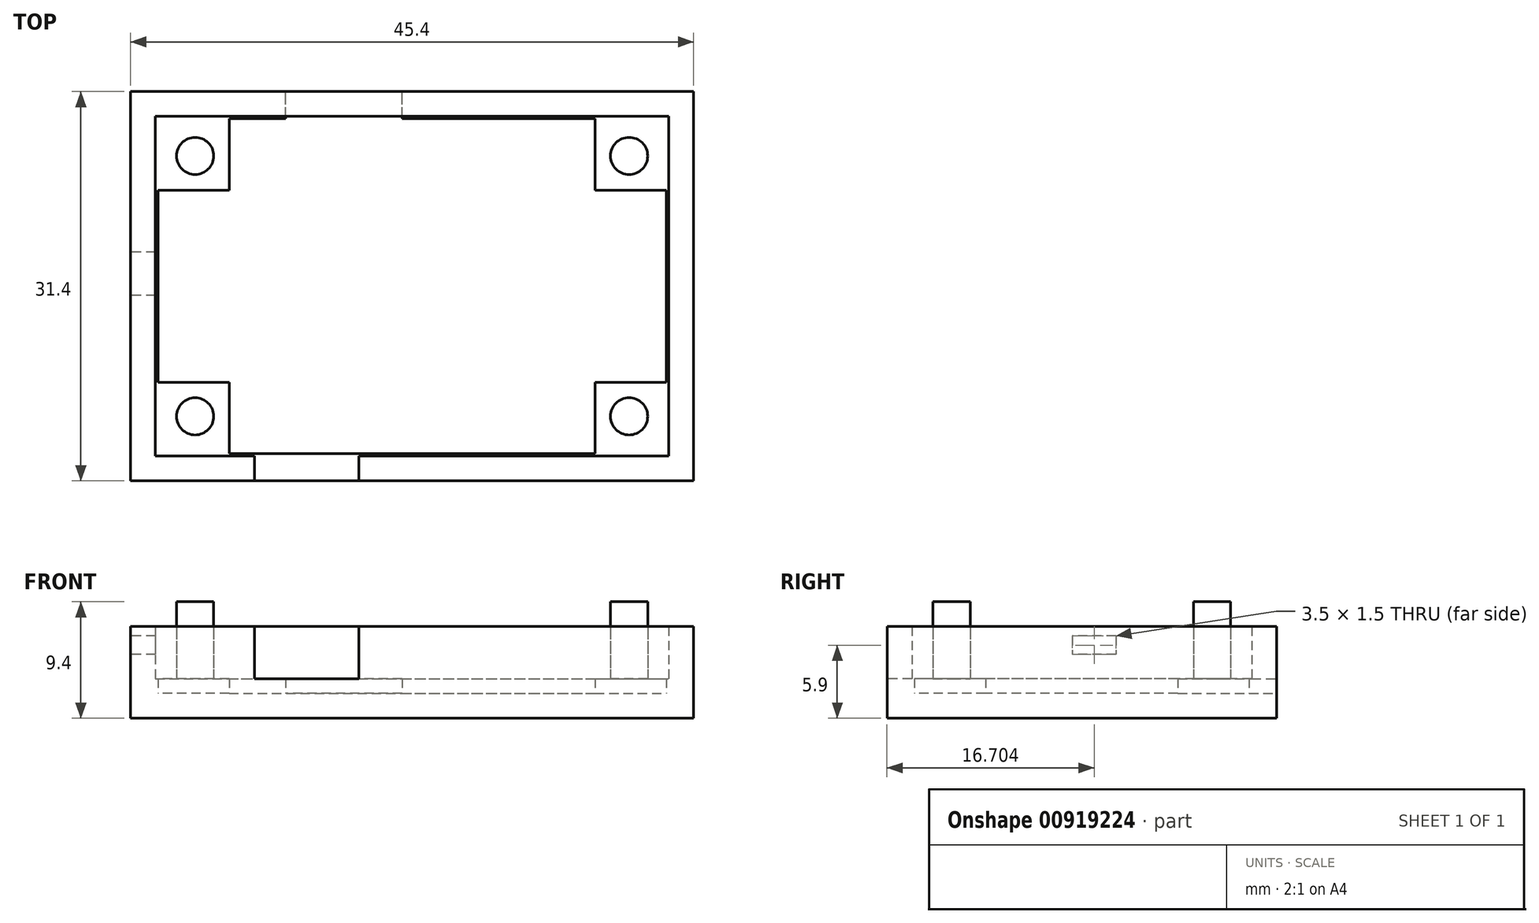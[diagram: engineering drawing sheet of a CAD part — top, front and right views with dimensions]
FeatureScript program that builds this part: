
annotation { "Feature Type Name" : "Feature", "Feature Type Description" : "" }
export const myFeature = defineFeature(function(context is Context, id is Id, definition is map)
    precondition{}
    {
        {
            assignVariable(context, id + "F0", {"name" : "thickness", "anyValue" : 2});
        }
        {
            assignVariable(context, id + "F1", {"name" : "padding", "anyValue" : 0.2});
        }
        {
            var Q0;
            Q0=qCreatedBy(makeId("Top.planeOp"),FACE);
            var sketch = newSketch(context, id + "F2", { "sketchPlane" : qUnion([Q0])});
            skLineSegment(sketch, "E0.bottom", {"start": v(-15.97, 10.74) * mm, "end": v(25.03, 10.74) * mm});
            skLineSegment(sketch, "E0.top", {"start": v(-15.97, -16.26) * mm, "end": v(25.03, -16.26) * mm});
            skLineSegment(sketch, "E0.left", {"start": v(-15.97, 10.74) * mm, "end": v(-15.97, -16.26) * mm});
            skLineSegment(sketch, "E0.right", {"start": v(25.03, 10.74) * mm, "end": v(25.03, -16.26) * mm});
            skCircle(sketch, "E1", {"center": v(-12.97, 7.74) * mm, "radius": 1.75 * mm});
            skPoint(sketch, "E2", {"position": v(25.03, -2.76) * mm});
            skCircle(sketch, "E3", {"center": v(22.03, 7.74) * mm, "radius": 1.75 * mm});
            skCircle(sketch, "E4", {"center": v(22.03, -13.26) * mm, "radius": 1.75 * mm});
            skCircle(sketch, "E5", {"center": v(-12.97, -13.26) * mm, "radius": 1.75 * mm});
            skLineSegment(sketch, "E6.bottom", {"start": v(-15.97, 10.74) * mm, "end": v(-10.22, 10.74) * mm});
            skLineSegment(sketch, "E6.top", {"start": v(-15.97, 5) * mm, "end": v(-10.22, 5) * mm});
            skLineSegment(sketch, "E6.left", {"start": v(-15.97, 10.74) * mm, "end": v(-15.97, 5) * mm});
            skLineSegment(sketch, "E6.right", {"start": v(-10.22, 10.74) * mm, "end": v(-10.22, 5) * mm});
            skLineSegment(sketch, "E7.bottom", {"start": v(19.28, 5) * mm, "end": v(25.03, 5) * mm});
            skLineSegment(sketch, "E7.top", {"start": v(19.28, 10.74) * mm, "end": v(25.03, 10.74) * mm});
            skLineSegment(sketch, "E7.left", {"start": v(19.28, 5) * mm, "end": v(19.28, 10.74) * mm});
            skLineSegment(sketch, "E7.right", {"start": v(25.03, 5) * mm, "end": v(25.03, 10.74) * mm});
            skLineSegment(sketch, "E8.bottom", {"start": v(19.28, -10.5) * mm, "end": v(25.03, -10.5) * mm});
            skLineSegment(sketch, "E8.top", {"start": v(19.28, -16.26) * mm, "end": v(25.03, -16.26) * mm});
            skLineSegment(sketch, "E8.left", {"start": v(19.28, -10.5) * mm, "end": v(19.28, -16.26) * mm});
            skLineSegment(sketch, "E8.right", {"start": v(25.03, -10.5) * mm, "end": v(25.03, -16.26) * mm});
            skLineSegment(sketch, "E9.bottom", {"start": v(-10.22, -10.5) * mm, "end": v(-15.97, -10.5) * mm});
            skLineSegment(sketch, "E9.top", {"start": v(-10.22, -16.26) * mm, "end": v(-15.97, -16.26) * mm});
            skLineSegment(sketch, "E9.left", {"start": v(-10.22, -10.5) * mm, "end": v(-10.22, -16.26) * mm});
            skLineSegment(sketch, "E9.right", {"start": v(-15.97, -10.5) * mm, "end": v(-15.97, -16.26) * mm});
            skLineSegment(sketch, "E10.bottom", {"start": v(-16.17, 10.94) * mm, "end": v(25.23, 10.94) * mm});
            skLineSegment(sketch, "E10.top", {"start": v(-16.17, -16.46) * mm, "end": v(25.23, -16.46) * mm});
            skLineSegment(sketch, "E10.left", {"start": v(-16.17, 10.94) * mm, "end": v(-16.17, -16.46) * mm});
            skLineSegment(sketch, "E10.right", {"start": v(25.23, 10.94) * mm, "end": v(25.23, -16.46) * mm});
            skLineSegment(sketch, "E11", {"start": v(19.28, 10.74) * mm, "end": v(19.28, 10.94) * mm});
            skLineSegment(sketch, "E12", {"start": v(25.03, 5) * mm, "end": v(25.23, 5) * mm});
            skLineSegment(sketch, "E13", {"start": v(-10.22, 10.74) * mm, "end": v(-10.22, 10.94) * mm});
            skLineSegment(sketch, "E14", {"start": v(-15.97, 5) * mm, "end": v(-16.17, 5) * mm});
            skLineSegment(sketch, "E15", {"start": v(-10.22, -16.26) * mm, "end": v(-10.22, -16.46) * mm});
            skLineSegment(sketch, "E16", {"start": v(-15.97, -10.5) * mm, "end": v(-16.17, -10.5) * mm});
            skLineSegment(sketch, "E17", {"start": v(19.28, -16.26) * mm, "end": v(19.28, -16.46) * mm});
            skLineSegment(sketch, "E18", {"start": v(25.03, -10.5) * mm, "end": v(25.23, -10.5) * mm});
            skLineSegment(sketch, "E19.bottom", {"start": v(-18.17, 12.94) * mm, "end": v(27.23, 12.94) * mm});
            skLineSegment(sketch, "E19.top", {"start": v(-18.17, -18.46) * mm, "end": v(27.23, -18.46) * mm});
            skLineSegment(sketch, "E19.left", {"start": v(-18.17, 12.94) * mm, "end": v(-18.17, -18.46) * mm});
            skLineSegment(sketch, "E19.right", {"start": v(27.23, 12.94) * mm, "end": v(27.23, -18.46) * mm});
            skSolve(sketch);
        }
        {
            var Q0;
            Q0=makeQuery(id+"F2.imprint","IMPRINT",FACE,{"disambiguationData":[TD([[makeQuery(id+"F2.imprint","IMPRINT",EDGE,{"derivedFrom":sQuery(id+"F2.wireOp",EDGE,"E3")}),-1.0]])]});
            var Q1;
            Q1=makeQuery(id+"F2.imprint","IMPRINT",FACE,{"disambiguationData":[TD([[makeQuery(id+"F2.imprint","IMPRINT",EDGE,{"derivedFrom":sQuery(id+"F2.wireOp",EDGE,"E1")}),-1.0]])]});
            var Q2;
            Q2=makeQuery(id+"F2.imprint","IMPRINT",FACE,{"disambiguationData":[TD([[makeQuery(id+"F2.imprint","IMPRINT",EDGE,{"derivedFrom":sQuery(id+"F2.wireOp",EDGE,"E1")}),1.0]])]});
            var Q3;
            Q3=makeQuery(id+"F2.imprint","IMPRINT",FACE,{"disambiguationData":[TD([[makeQuery(id+"F2.imprint","IMPRINT",EDGE,{"derivedFrom":sQuery(id+"F2.wireOp",EDGE,"E3")}),1.0]])]});
            var Q4;
            Q4=makeQuery(id+"F2.imprint","IMPRINT",FACE,{"disambiguationData":[TD([[makeQuery(id+"F2.imprint","IMPRINT",EDGE,{"derivedFrom":sQuery(id+"F2.wireOp",EDGE,"E4")}),1.0]])]});
            var Q5;
            Q5=makeQuery(id+"F2.imprint","IMPRINT",FACE,{"disambiguationData":[TD([[makeQuery(id+"F2.imprint","IMPRINT",EDGE,{"derivedFrom":sQuery(id+"F2.wireOp",EDGE,"E4")}),-1.0]])]});
            var Q6;
            Q6=makeQuery(id+"F2.imprint","IMPRINT",FACE,{"disambiguationData":[TD([[makeQuery(id+"F2.imprint","IMPRINT",EDGE,{"derivedFrom":sQuery(id+"F2.wireOp",EDGE,"E5")}),1.0]])]});
            var Q7;
            Q7=makeQuery(id+"F2.imprint","IMPRINT",FACE,{"disambiguationData":[TD([[makeQuery(id+"F2.imprint","IMPRINT",EDGE,{"derivedFrom":sQuery(id+"F2.wireOp",EDGE,"E5")}),-1.0]])]});
            var Q8;
            {var subQ0=sQuery(id+"F2.wireOp",EDGE,"E15");Q8=makeQuery(id+"F2.imprint","IMPRINT",FACE,{"disambiguationData":[TD([[makeQuery(id+"F2.imprint","IMPRINT",EDGE,{"derivedFrom":subQ0}),1.0]])]});}
            var Q9;
            {var subQ4=sQuery(id+"F2.wireOp",EDGE,"E15");Q9=makeQuery(id+"F2.imprint","IMPRINT",FACE,{"disambiguationData":[TD([[makeQuery(id+"F2.imprint","IMPRINT",EDGE,{"derivedFrom":subQ4}),-1.0]])]});}
            var Q10;
            {var subQ0=sQuery(id+"F2.wireOp",EDGE,"E14");Q10=makeQuery(id+"F2.imprint","IMPRINT",FACE,{"disambiguationData":[TD([[makeQuery(id+"F2.imprint","IMPRINT",EDGE,{"derivedFrom":subQ0}),1.0]])]});}
            var Q11;
            {var subQ0=sQuery(id+"F2.wireOp",EDGE,"E13");Q11=makeQuery(id+"F2.imprint","IMPRINT",FACE,{"disambiguationData":[TD([[makeQuery(id+"F2.imprint","IMPRINT",EDGE,{"derivedFrom":subQ0}),1.0]])]});}
            var Q12;
            {var subQ2=sQuery(id+"F2.wireOp",EDGE,"E11");Q12=makeQuery(id+"F2.imprint","IMPRINT",FACE,{"disambiguationData":[TD([[makeQuery(id+"F2.imprint","IMPRINT",EDGE,{"derivedFrom":subQ2}),1.0]])]});}
            var Q13;
            {var subQ0=sQuery(id+"F2.wireOp",EDGE,"E12");Q13=makeQuery(id+"F2.imprint","IMPRINT",FACE,{"disambiguationData":[TD([[makeQuery(id+"F2.imprint","IMPRINT",EDGE,{"derivedFrom":subQ0}),-1.0]])]});}
            var Q14;
            {var subQ3=sQuery(id+"F2.wireOp",EDGE,"E17");Q14=makeQuery(id+"F2.imprint","IMPRINT",FACE,{"disambiguationData":[TD([[makeQuery(id+"F2.imprint","IMPRINT",EDGE,{"derivedFrom":subQ3}),1.0]])]});}
            var Q15;
            Q15=makeQuery(id+"F2.imprint","IMPRINT",FACE,{"disambiguationData":[TD([[makeQuery(id+"F2.imprint","IMPRINT",EDGE,{"derivedFrom":sQuery(id+"F2.wireOp",EDGE,"E19.bottom")}),-1.0]])]});
            var Q16;
            {var subQ4=sQuery(id+"F2.wireOp",EDGE,"E11");Q16=makeQuery(id+"F2.imprint","IMPRINT",FACE,{"disambiguationData":[TD([[makeQuery(id+"F2.imprint","IMPRINT",EDGE,{"derivedFrom":subQ4}),-1.0]])]});}
            extrude(context, id + "F3", {"entities" : qUnion([Q0, Q1, Q2, Q3, Q4, Q5, Q6, Q7, Q8, Q9, Q10, Q11, Q12, Q13, Q14, Q15, Q16]), "depth" : (1 + getVariable(context, 'padding')) * mm, "offsetDistance" : 25 * mm});
        }
        {
            var Q0;
            Q0=makeQuery(id+"F2.imprint","IMPRINT",FACE,{"disambiguationData":[TD([[makeQuery(id+"F2.imprint","IMPRINT",EDGE,{"derivedFrom":sQuery(id+"F2.wireOp",EDGE,"E1")}),1.0]])]});
            var Q1;
            Q1=makeQuery(id+"F2.imprint","IMPRINT",FACE,{"disambiguationData":[TD([[makeQuery(id+"F2.imprint","IMPRINT",EDGE,{"derivedFrom":sQuery(id+"F2.wireOp",EDGE,"E1")}),-1.0]])]});
            var Q2;
            {var subQ0=sQuery(id+"F2.wireOp",EDGE,"E13");Q2=makeQuery(id+"F2.imprint","IMPRINT",FACE,{"disambiguationData":[TD([[makeQuery(id+"F2.imprint","IMPRINT",EDGE,{"derivedFrom":subQ0}),1.0]])]});}
            var Q3;
            {var subQ2=sQuery(id+"F2.wireOp",EDGE,"E11");Q3=makeQuery(id+"F2.imprint","IMPRINT",FACE,{"disambiguationData":[TD([[makeQuery(id+"F2.imprint","IMPRINT",EDGE,{"derivedFrom":subQ2}),1.0]])]});}
            var Q4;
            {var subQ0=sQuery(id+"F2.wireOp",EDGE,"E14");Q4=makeQuery(id+"F2.imprint","IMPRINT",FACE,{"disambiguationData":[TD([[makeQuery(id+"F2.imprint","IMPRINT",EDGE,{"derivedFrom":subQ0}),1.0]])]});}
            var Q5;
            {var subQ4=sQuery(id+"F2.wireOp",EDGE,"E15");Q5=makeQuery(id+"F2.imprint","IMPRINT",FACE,{"disambiguationData":[TD([[makeQuery(id+"F2.imprint","IMPRINT",EDGE,{"derivedFrom":subQ4}),-1.0]])]});}
            var Q6;
            {var subQ0=sQuery(id+"F2.wireOp",EDGE,"E15");Q6=makeQuery(id+"F2.imprint","IMPRINT",FACE,{"disambiguationData":[TD([[makeQuery(id+"F2.imprint","IMPRINT",EDGE,{"derivedFrom":subQ0}),1.0]])]});}
            var Q7;
            Q7=makeQuery(id+"F2.imprint","IMPRINT",FACE,{"disambiguationData":[TD([[makeQuery(id+"F2.imprint","IMPRINT",EDGE,{"derivedFrom":sQuery(id+"F2.wireOp",EDGE,"E5")}),1.0]])]});
            var Q8;
            Q8=makeQuery(id+"F2.imprint","IMPRINT",FACE,{"disambiguationData":[TD([[makeQuery(id+"F2.imprint","IMPRINT",EDGE,{"derivedFrom":sQuery(id+"F2.wireOp",EDGE,"E5")}),-1.0]])]});
            var Q9;
            Q9=makeQuery(id+"F2.imprint","IMPRINT",FACE,{"disambiguationData":[TD([[makeQuery(id+"F2.imprint","IMPRINT",EDGE,{"derivedFrom":sQuery(id+"F2.wireOp",EDGE,"E4")}),-1.0]])]});
            var Q10;
            Q10=makeQuery(id+"F2.imprint","IMPRINT",FACE,{"disambiguationData":[TD([[makeQuery(id+"F2.imprint","IMPRINT",EDGE,{"derivedFrom":sQuery(id+"F2.wireOp",EDGE,"E4")}),1.0]])]});
            var Q11;
            {var subQ3=sQuery(id+"F2.wireOp",EDGE,"E17");Q11=makeQuery(id+"F2.imprint","IMPRINT",FACE,{"disambiguationData":[TD([[makeQuery(id+"F2.imprint","IMPRINT",EDGE,{"derivedFrom":subQ3}),1.0]])]});}
            var Q12;
            Q12=makeQuery(id+"F2.imprint","IMPRINT",FACE,{"disambiguationData":[TD([[makeQuery(id+"F2.imprint","IMPRINT",EDGE,{"derivedFrom":sQuery(id+"F2.wireOp",EDGE,"E19.bottom")}),-1.0]])]});
            var Q13;
            {var subQ0=sQuery(id+"F2.wireOp",EDGE,"E12");Q13=makeQuery(id+"F2.imprint","IMPRINT",FACE,{"disambiguationData":[TD([[makeQuery(id+"F2.imprint","IMPRINT",EDGE,{"derivedFrom":subQ0}),-1.0]])]});}
            var Q14;
            {var subQ4=sQuery(id+"F2.wireOp",EDGE,"E11");Q14=makeQuery(id+"F2.imprint","IMPRINT",FACE,{"disambiguationData":[TD([[makeQuery(id+"F2.imprint","IMPRINT",EDGE,{"derivedFrom":subQ4}),-1.0]])]});}
            var Q15;
            Q15=makeQuery(id+"F2.imprint","IMPRINT",FACE,{"disambiguationData":[TD([[makeQuery(id+"F2.imprint","IMPRINT",EDGE,{"derivedFrom":sQuery(id+"F2.wireOp",EDGE,"E3")}),1.0]])]});
            var Q16;
            Q16=makeQuery(id+"F2.imprint","IMPRINT",FACE,{"disambiguationData":[TD([[makeQuery(id+"F2.imprint","IMPRINT",EDGE,{"derivedFrom":sQuery(id+"F2.wireOp",EDGE,"E3")}),-1.0]])]});
            var Q17;
            {var subQ3=sQuery(id+"F2.wireOp",EDGE,"E6.top");Q17=makeQuery(id+"F2.imprint","IMPRINT",FACE,{"disambiguationData":[TD([[makeQuery(id+"F2.imprint","IMPRINT",EDGE,{"derivedFrom":subQ3}),-1.0]])]});}
            extrude(context, id + "F4", {"entities" : qUnion([Q0, Q1, Q2, Q3, Q4, Q5, Q6, Q7, Q8, Q9, Q10, Q11, Q12, Q13, Q14, Q15, Q16, Q17]), "operationType" : NewBodyOperationType.ADD, "oppositeDirection" : true, "depth" : (getVariable(context, 'thickness')) * mm, "offsetDistance" : 25 * mm});
        }
        {
            var Q0;
            Q0=makeQuery(id+"F3.opExtrude","CAP_FACE",FACE,{"disambiguationData":[OSD([sQuery(id+"F2.wireOp",EDGE,"E0.bottom"),sQuery(id+"F2.wireOp",EDGE,"E0.top"),sQuery(id+"F2.wireOp",EDGE,"E0.left"),sQuery(id+"F2.wireOp",EDGE,"E0.right"),sQuery(id+"F2.wireOp",EDGE,"E6.top"),sQuery(id+"F2.wireOp",EDGE,"E6.right"),sQuery(id+"F2.wireOp",EDGE,"E7.bottom"),sQuery(id+"F2.wireOp",EDGE,"E7.left"),sQuery(id+"F2.wireOp",EDGE,"E8.bottom"),sQuery(id+"F2.wireOp",EDGE,"E8.left"),sQuery(id+"F2.wireOp",EDGE,"E9.bottom"),sQuery(id+"F2.wireOp",EDGE,"E9.left"),sQuery(id+"F2.wireOp",EDGE,"E19.bottom"),sQuery(id+"F2.wireOp",EDGE,"E19.top"),sQuery(id+"F2.wireOp",EDGE,"E19.left"),sQuery(id+"F2.wireOp",EDGE,"E19.right")])],"isStart":false});
            var sketch = newSketch(context, id + "F5", { "sketchPlane" : qUnion([Q0])});
            skPoint(sketch, "E20", {"position": v(-12.97, 7.74) * mm});
            skPoint(sketch, "E21", {"position": v(22.03, 7.74) * mm});
            skPoint(sketch, "E22", {"position": v(22.03, -13.26) * mm});
            skPoint(sketch, "E23", {"position": v(-12.97, -13.26) * mm});
            skCircle(sketch, "E24", {"center": v(-12.97, 7.74) * mm, "radius": 1.5 * mm});
            skCircle(sketch, "E25", {"center": v(22.03, 7.74) * mm, "radius": 1.5 * mm});
            skCircle(sketch, "E26", {"center": v(22.03, -13.26) * mm, "radius": 1.5 * mm});
            skCircle(sketch, "E27", {"center": v(-12.97, -13.26) * mm, "radius": 1.5 * mm});
            skLineSegment(sketch, "E28.bottom", {"start": v(-16.17, 10.94) * mm, "end": v(25.23, 10.94) * mm});
            skLineSegment(sketch, "E28.top", {"start": v(-16.17, -16.46) * mm, "end": v(25.23, -16.46) * mm});
            skLineSegment(sketch, "E28.left", {"start": v(-16.17, 10.94) * mm, "end": v(-16.17, -16.46) * mm});
            skLineSegment(sketch, "E28.right", {"start": v(25.23, 10.94) * mm, "end": v(25.23, -16.46) * mm});
            skLineSegment(sketch, "E29.bottom", {"start": v(-18.17, 12.94) * mm, "end": v(27.23, 12.94) * mm});
            skLineSegment(sketch, "E29.top", {"start": v(-18.17, -18.46) * mm, "end": v(27.23, -18.46) * mm});
            skLineSegment(sketch, "E29.left", {"start": v(-18.17, 12.94) * mm, "end": v(-18.17, -18.46) * mm});
            skLineSegment(sketch, "E29.right", {"start": v(27.23, 12.94) * mm, "end": v(27.23, -18.46) * mm});
            skSolve(sketch);
        }
        {
            var Q0;
            Q0 = qSketchRegion(id + "F5", true);
            extrude(context, id + "F6", {"entities" : qUnion([Q0]), "operationType" : NewBodyOperationType.ADD, "depth" : (4 + getVariable(context, 'padding')) * mm, "offsetDistance" : 25 * mm});
        }
        {
            var Q0;
            Q0=makeQuery(id+"F5.imprint","IMPRINT",FACE,{"disambiguationData":[TD([[makeQuery(id+"F5.imprint","IMPRINT",EDGE,{"derivedFrom":sQuery(id+"F5.wireOp",EDGE,"E24")}),1.0]])]});
            var Q1;
            Q1=makeQuery(id+"F5.imprint","IMPRINT",FACE,{"disambiguationData":[TD([[makeQuery(id+"F5.imprint","IMPRINT",EDGE,{"derivedFrom":sQuery(id+"F5.wireOp",EDGE,"E25")}),1.0]])]});
            var Q2;
            Q2=makeQuery(id+"F5.imprint","IMPRINT",FACE,{"disambiguationData":[TD([[makeQuery(id+"F5.imprint","IMPRINT",EDGE,{"derivedFrom":sQuery(id+"F5.wireOp",EDGE,"E26")}),1.0]])]});
            var Q3;
            Q3=makeQuery(id+"F5.imprint","IMPRINT",FACE,{"disambiguationData":[TD([[makeQuery(id+"F5.imprint","IMPRINT",EDGE,{"derivedFrom":sQuery(id+"F5.wireOp",EDGE,"E27")}),1.0]])]});
            extrude(context, id + "F7", {"entities" : qUnion([Q0, Q1, Q2, Q3]), "operationType" : NewBodyOperationType.ADD, "depth" : (4 + getVariable(context, 'padding') + getVariable(context, 'thickness')) * mm, "offsetDistance" : 25 * mm});
        }
        {
            var Q0;
            {var subQ0=sQuery(id+"F2.wireOp",EDGE,"E19.left");Q0=makeQuery(id+"F6.boolean.opBoolean","MERGE",FACE,{"derivedFrom":[makeQuery(id+"F4.boolean.opBoolean","MERGE",FACE,{"derivedFrom":[makeQuery(id+"F3.opExtrude","SWEPT_FACE",FACE,{"disambiguationData":[OSD([subQ0])]}),makeQuery(id+"F4.opExtrude","SWEPT_FACE",FACE,{"disambiguationData":[OSD([subQ0])]})]}),makeQuery(id+"F6.opExtrude","SWEPT_FACE",FACE,{"disambiguationData":[OSD([sQuery(id+"F5.wireOp",EDGE,"E29.left")])]})]});}
            var sketch = newSketch(context, id + "F8", { "sketchPlane" : qUnion([Q0])});
            skLineSegment(sketch, "E30.bottom", {"start": v(0, 4.65) * mm, "end": v(3.5, 4.65) * mm});
            skLineSegment(sketch, "E30.top", {"start": v(0, 3.15) * mm, "end": v(3.5, 3.15) * mm});
            skLineSegment(sketch, "E30.left", {"start": v(0, 4.65) * mm, "end": v(0, 3.15) * mm});
            skLineSegment(sketch, "E30.right", {"start": v(3.5, 4.65) * mm, "end": v(3.5, 3.15) * mm});
            skSolve(sketch);
        }
        {
            var Q0;
            Q0 = qSketchRegion(id + "F8", true);
            extrude(context, id + "F9", {"entities" : qUnion([Q0]), "operationType" : NewBodyOperationType.REMOVE, "endBound" : BoundingType.UP_TO_NEXT, "oppositeDirection" : true, "depth" : 25 * mm, "offsetDistance" : 25 * mm});
        }
        {
            var Q0;
            {var subQ0=sQuery(id+"F2.wireOp",EDGE,"E19.top");Q0=makeQuery(id+"F6.boolean.opBoolean","MERGE",FACE,{"derivedFrom":[makeQuery(id+"F4.boolean.opBoolean","MERGE",FACE,{"derivedFrom":[makeQuery(id+"F3.opExtrude","SWEPT_FACE",FACE,{"disambiguationData":[OSD([subQ0])]}),makeQuery(id+"F4.opExtrude","SWEPT_FACE",FACE,{"disambiguationData":[OSD([subQ0])]})]}),makeQuery(id+"F6.opExtrude","SWEPT_FACE",FACE,{"disambiguationData":[OSD([sQuery(id+"F5.wireOp",EDGE,"E29.top")])]})]});}
            var sketch = newSketch(context, id + "F10", { "sketchPlane" : qUnion([Q0])});
            skLineSegment(sketch, "E31.bottom", {"start": v(-8.17, 5.4) * mm, "end": v(0.23, 5.4) * mm});
            skLineSegment(sketch, "E31.top", {"start": v(-8.17, 1.2) * mm, "end": v(0.23, 1.2) * mm});
            skLineSegment(sketch, "E31.left", {"start": v(-8.17, 5.4) * mm, "end": v(-8.17, 1.2) * mm});
            skLineSegment(sketch, "E31.right", {"start": v(0.23, 5.4) * mm, "end": v(0.23, 1.2) * mm});
            skSolve(sketch);
        }
        {
            var Q0;
            Q0 = qSketchRegion(id + "F10", true);
            extrude(context, id + "F11", {"entities" : qUnion([Q0]), "operationType" : NewBodyOperationType.REMOVE, "endBound" : BoundingType.UP_TO_NEXT, "oppositeDirection" : true, "depth" : 25 * mm, "offsetDistance" : 25 * mm});
        }
        {
            var Q0;
            {var subQ0=sQuery(id+"F2.wireOp",EDGE,"E19.bottom");Q0=makeQuery(id+"F6.boolean.opBoolean","MERGE",FACE,{"derivedFrom":[makeQuery(id+"F4.boolean.opBoolean","MERGE",FACE,{"derivedFrom":[makeQuery(id+"F3.opExtrude","SWEPT_FACE",FACE,{"disambiguationData":[OSD([subQ0])]}),makeQuery(id+"F4.opExtrude","SWEPT_FACE",FACE,{"disambiguationData":[OSD([subQ0])]})]}),makeQuery(id+"F6.opExtrude","SWEPT_FACE",FACE,{"disambiguationData":[OSD([sQuery(id+"F5.wireOp",EDGE,"E29.bottom")])]})]});}
            var sketch = newSketch(context, id + "F12", { "sketchPlane" : qUnion([Q0])});
            skLineSegment(sketch, "E32.bottom", {"start": v(-3.73, 0) * mm, "end": v(5.67, 0) * mm});
            skLineSegment(sketch, "E32.top", {"start": v(-3.73, 1.2) * mm, "end": v(5.67, 1.2) * mm});
            skLineSegment(sketch, "E32.left", {"start": v(-3.73, 0) * mm, "end": v(-3.73, 1.2) * mm});
            skLineSegment(sketch, "E32.right", {"start": v(5.67, 0) * mm, "end": v(5.67, 1.2) * mm});
            skSolve(sketch);
        }
        {
            var Q0;
            Q0=makeQuery(id+"F12.imprint","IMPRINT",FACE,{"disambiguationData":[TD([[makeQuery(id+"F12.imprint","IMPRINT",EDGE,{"derivedFrom":sQuery(id+"F12.wireOp",EDGE,"E32.bottom")}),1.0]])]});
            extrude(context, id + "F13", {"entities" : qUnion([Q0]), "operationType" : NewBodyOperationType.REMOVE, "endBound" : BoundingType.UP_TO_NEXT, "oppositeDirection" : true, "depth" : 25 * mm, "offsetDistance" : 25 * mm});
        }
    });
